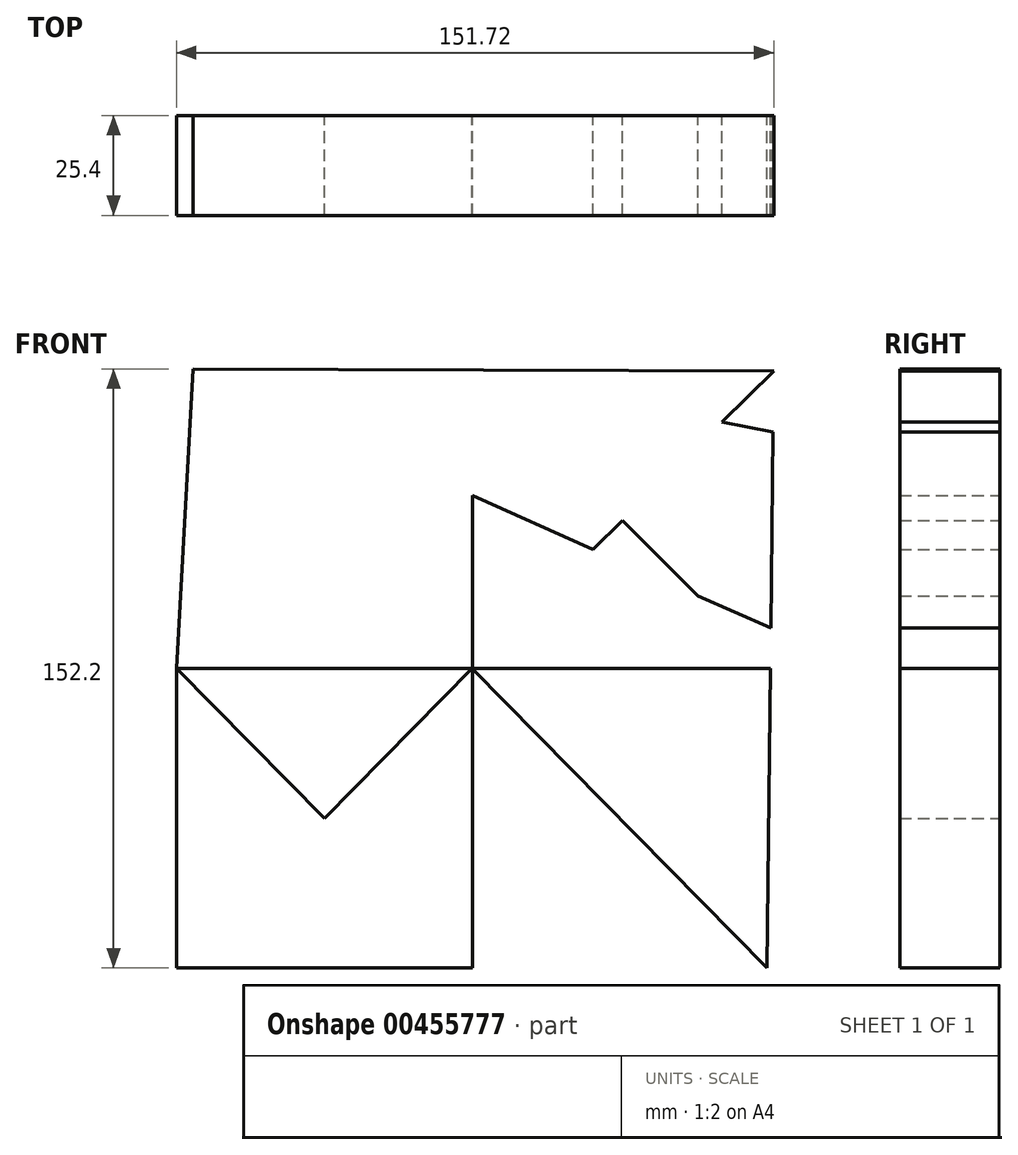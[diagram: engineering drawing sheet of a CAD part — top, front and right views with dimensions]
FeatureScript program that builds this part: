
annotation { "Feature Type Name" : "Feature", "Feature Type Description" : "" }
export const myFeature = defineFeature(function(context is Context, id is Id, definition is map)
    precondition{}
    {
        {
            var Q0;
            Q0=qCreatedBy(makeId("Front.planeOp"),FACE);
            var sketch = newSketch(context, id + "F0", { "sketchPlane" : qUnion([Q0])});
            skLineSegment(sketch, "E0", {"start": v(-75.13, 76.1) * mm, "end": v(74.89, -76.1) * mm});
            skLineSegment(sketch, "E1", {"start": v(74.89, -76.1) * mm, "end": v(76.6, 75.62) * mm});
            skLineSegment(sketch, "E2", {"start": v(76.6, 75.62) * mm, "end": v(-75.13, 76.1) * mm});
            skLineSegment(sketch, "E3", {"start": v(-75.13, 75.62) * mm, "end": v(-75.13, -76.1) * mm});
            skLineSegment(sketch, "E4", {"start": v(-75.13, -76.1) * mm, "end": v(74.89, -76.1) * mm});
            skLineSegment(sketch, "E5", {"start": v(0, 0) * mm, "end": v(-75.13, -76.1) * mm});
            skLineSegment(sketch, "E6", {"start": v(-75.13, -76.1) * mm, "end": v(-75.13, 75.62) * mm});
            skLineSegment(sketch, "E7", {"start": v(0, 0) * mm, "end": v(-75.13, 0) * mm});
            skLineSegment(sketch, "E8", {"start": v(-75.13, 0) * mm, "end": v(-70.98, 76.1) * mm});
            skLineSegment(sketch, "E9", {"start": v(-70.98, 76.1) * mm, "end": v(-75.13, 71.9) * mm});
            skLineSegment(sketch, "E10", {"start": v(-75.13, 71.9) * mm, "end": v(-71.45, 75.62) * mm});
            skLineSegment(sketch, "E11", {"start": v(-71.45, 75.62) * mm, "end": v(75.86, 10.23) * mm});
            skLineSegment(sketch, "E12", {"start": v(75.86, 10.23) * mm, "end": v(0, 0) * mm});
            skLineSegment(sketch, "E13", {"start": v(0, 0) * mm, "end": v(76.6, 75.62) * mm});
            skLineSegment(sketch, "E14", {"start": v(0, 75.87) * mm, "end": v(0, -76.1) * mm});
            skLineSegment(sketch, "E15", {"start": v(0, -76.1) * mm, "end": v(-75.13, 0) * mm});
            skLineSegment(sketch, "E16", {"start": v(-75.13, 0) * mm, "end": v(75.86, 0) * mm});
            skLineSegment(sketch, "E17", {"start": v(75.86, 0) * mm, "end": v(0, 75.62) * mm});
            skLineSegment(sketch, "E18", {"start": v(0, 75.62) * mm, "end": v(76.42, 60.01) * mm});
            skSolve(sketch);
        }
        {
            var Q0;
            {var subQ5=sQuery(id+"F0.wireOp",EDGE,"E8");var subQ7=sQuery(id+"F0.wireOp",EDGE,"E0");var subQ8=makeQuery(id+"F0.imprint","INTERSECT",VERTEX,{"derivedFrom":[subQ7,subQ5]});Q0=makeQuery(id+"F0.imprint","IMPRINT",FACE,{"disambiguationData":[TD([[makeQuery(id+"F0.imprint","IMPRINT",EDGE,{"disambiguationData":[TD([[subQ8,-1.0]])],"derivedFrom":subQ7}),1.0]])]});}
            var Q1;
            {var subQ0=sQuery(id+"F0.wireOp",EDGE,"E8");var subQ1=sQuery(id+"F0.wireOp",EDGE,"E0");var subQ2=makeQuery(id+"F0.imprint","INTERSECT",VERTEX,{"derivedFrom":[subQ1,subQ0]});Q1=makeQuery(id+"F0.imprint","IMPRINT",FACE,{"disambiguationData":[TD([[makeQuery(id+"F0.imprint","IMPRINT",EDGE,{"disambiguationData":[TD([[subQ2,-1.0]])],"derivedFrom":subQ1}),-1.0]])]});}
            var Q2;
            {var subQ4=sQuery(id+"F0.wireOp",EDGE,"E11");var subQ5=sQuery(id+"F0.wireOp",EDGE,"E8");var subQ6=makeQuery(id+"F0.imprint","INTERSECT",VERTEX,{"derivedFrom":[subQ5,subQ4]});Q2=makeQuery(id+"F0.imprint","IMPRINT",FACE,{"disambiguationData":[TD([[makeQuery(id+"F0.imprint","IMPRINT",EDGE,{"disambiguationData":[TD([[subQ6,-1.0]])],"derivedFrom":subQ4}),1.0]])]});}
            var Q3;
            {var subQ0=sQuery(id+"F0.wireOp",EDGE,"E14");var subQ1=sQuery(id+"F0.wireOp",EDGE,"E11");var subQ2=makeQuery(id+"F0.imprint","INTERSECT",VERTEX,{"derivedFrom":[subQ1,subQ0]});Q3=makeQuery(id+"F0.imprint","IMPRINT",FACE,{"disambiguationData":[TD([[makeQuery(id+"F0.imprint","IMPRINT",EDGE,{"disambiguationData":[TD([[subQ2,-1.0]])],"derivedFrom":subQ1}),1.0]])]});}
            var Q4;
            {var subQ0=sQuery(id+"F0.wireOp",EDGE,"E17");var subQ1=sQuery(id+"F0.wireOp",EDGE,"E13");var subQ2=makeQuery(id+"F0.imprint","INTERSECT",VERTEX,{"derivedFrom":[subQ1,subQ0]});Q4=makeQuery(id+"F0.imprint","IMPRINT",FACE,{"disambiguationData":[TD([[makeQuery(id+"F0.imprint","IMPRINT",EDGE,{"disambiguationData":[TD([[subQ2,-1.0]])],"derivedFrom":subQ1}),1.0]])]});}
            var Q5;
            {var subQ1=sQuery(id+"F0.wireOp",EDGE,"E2");var subQ3=sQuery(id+"F0.wireOp",EDGE,"E14");var subQ4=makeQuery(id+"F0.imprint","INTERSECT",VERTEX,{"derivedFrom":[subQ1,subQ3]});Q5=makeQuery(id+"F0.imprint","IMPRINT",FACE,{"disambiguationData":[TD([[makeQuery(id+"F0.imprint","IMPRINT",EDGE,{"disambiguationData":[TD([[subQ4,1.0]])],"derivedFrom":subQ1}),1.0]])]});}
            var Q6;
            {var subQ0=sQuery(id+"F0.wireOp",EDGE,"E17");var subQ3=sQuery(id+"F0.wireOp",EDGE,"E13");var subQ4=makeQuery(id+"F0.imprint","INTERSECT",VERTEX,{"derivedFrom":[subQ3,subQ0]});Q6=makeQuery(id+"F0.imprint","IMPRINT",FACE,{"disambiguationData":[TD([[makeQuery(id+"F0.imprint","IMPRINT",EDGE,{"disambiguationData":[TD([[subQ4,-1.0]])],"derivedFrom":subQ3}),-1.0]])]});}
            var Q7;
            {var subQ0=sQuery(id+"F0.wireOp",EDGE,"E5");var subQ1=sQuery(id+"F0.wireOp",EDGE,"E0");var subQ2=makeQuery(id+"F0.imprint","INTERSECT",VERTEX,{"derivedFrom":[subQ1,subQ0]});Q7=makeQuery(id+"F0.imprint","IMPRINT",FACE,{"disambiguationData":[TD([[makeQuery(id+"F0.imprint","IMPRINT",EDGE,{"disambiguationData":[TD([[subQ2,-1.0]])],"derivedFrom":subQ1}),-1.0]])]});}
            var Q8;
            {var subQ1=sQuery(id+"F0.wireOp",EDGE,"E5");var subQ3=sQuery(id+"F0.wireOp",EDGE,"E15");var subQ4=makeQuery(id+"F0.imprint","INTERSECT",VERTEX,{"derivedFrom":[subQ1,subQ3]});Q8=makeQuery(id+"F0.imprint","IMPRINT",FACE,{"disambiguationData":[TD([[makeQuery(id+"F0.imprint","IMPRINT",EDGE,{"disambiguationData":[TD([[subQ4,-1.0]])],"derivedFrom":subQ1}),-1.0]])]});}
            var Q9;
            {var subQ0=sQuery(id+"F0.wireOp",EDGE,"E5");var subQ3=sQuery(id+"F0.wireOp",EDGE,"E15");var subQ5=makeQuery(id+"F0.imprint","INTERSECT",VERTEX,{"derivedFrom":[subQ0,subQ3]});Q9=makeQuery(id+"F0.imprint","IMPRINT",FACE,{"disambiguationData":[TD([[makeQuery(id+"F0.imprint","IMPRINT",EDGE,{"disambiguationData":[TD([[subQ5,-1.0]])],"derivedFrom":subQ0}),1.0]])]});}
            var Q10;
            {var subQ1=sQuery(id+"F0.wireOp",EDGE,"E0");var subQ3=sQuery(id+"F0.wireOp",EDGE,"E14");var subQ4=makeQuery(id+"F0.imprint","INTERSECT",VERTEX,{"derivedFrom":[subQ1,subQ3]});Q10=makeQuery(id+"F0.imprint","IMPRINT",FACE,{"disambiguationData":[TD([[makeQuery(id+"F0.imprint","IMPRINT",EDGE,{"disambiguationData":[TD([[subQ4,-1.0]])],"derivedFrom":subQ1}),1.0]])]});}
            extrude(context, id + "F1", {"entities" : qUnion([Q0, Q1, Q2, Q3, Q4, Q5, Q6, Q7, Q8, Q9, Q10]), "depth" : 25.4 * mm});
        }
    });
